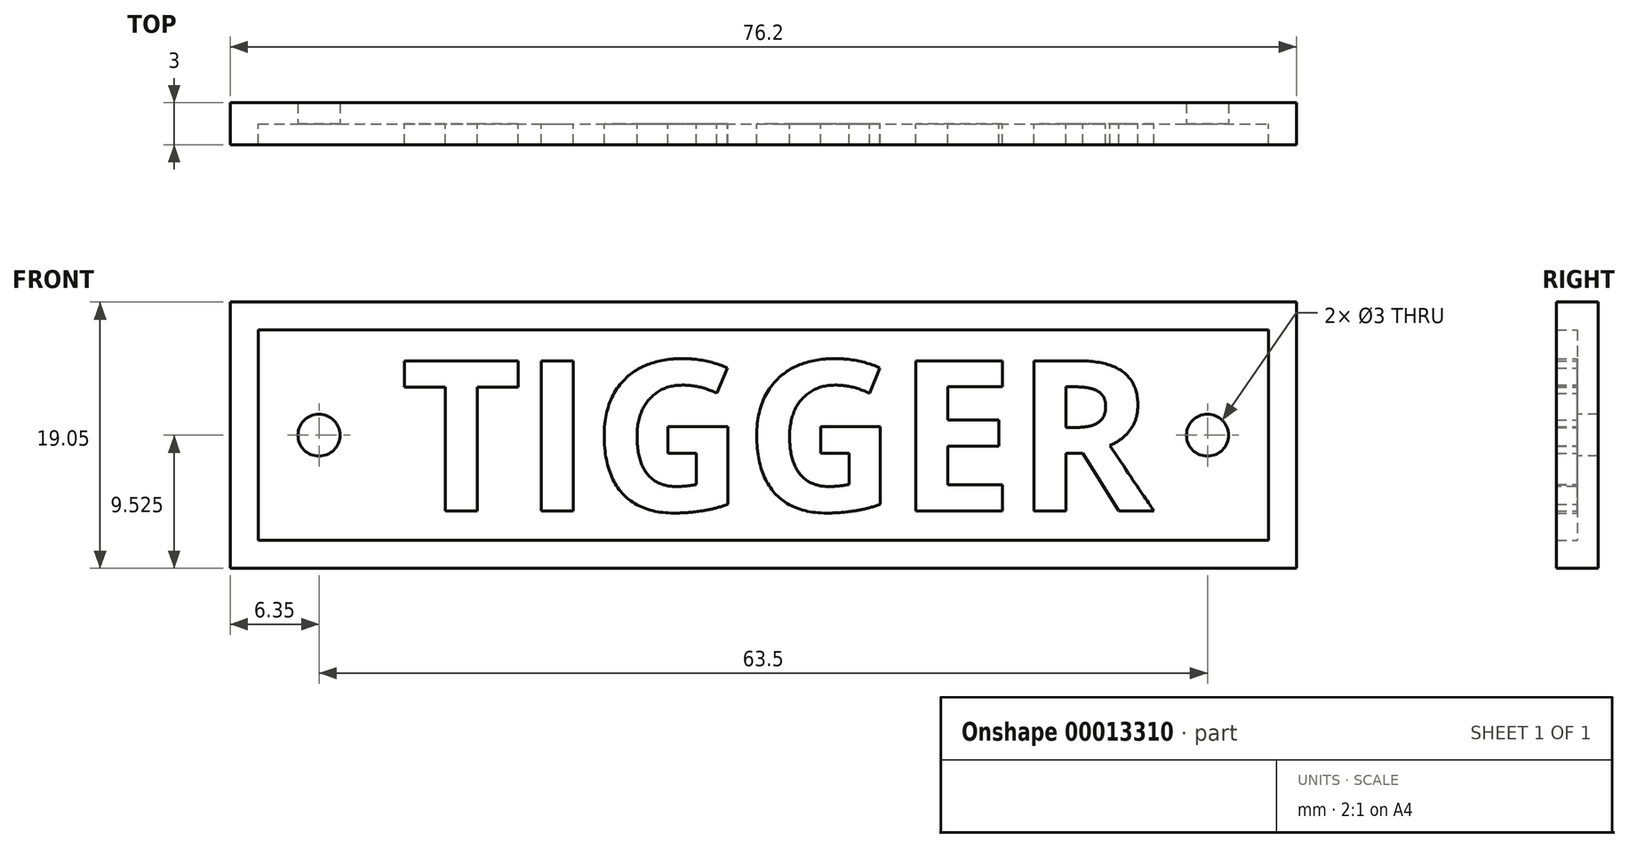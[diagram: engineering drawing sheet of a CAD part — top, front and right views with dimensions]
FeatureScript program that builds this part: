
annotation { "Feature Type Name" : "Feature", "Feature Type Description" : "" }
export const myFeature = defineFeature(function(context is Context, id is Id, definition is map)
    precondition{}
    {
        {
            var Q0;
            Q0=qCreatedBy(makeId("Front.planeOp"),FACE);
            var sketch = newSketch(context, id + "F0", { "sketchPlane" : qUnion([Q0])});
            skLineSegment(sketch, "E0.bottom", {"start": v(76.2, 19.05) * mm, "end": v(0, 19.05) * mm});
            skLineSegment(sketch, "E0.top", {"start": v(76.2, 0) * mm, "end": v(0, 0) * mm});
            skLineSegment(sketch, "E0.left", {"start": v(76.2, 19.05) * mm, "end": v(76.2, 0) * mm});
            skLineSegment(sketch, "E0.right", {"start": v(0, 19.05) * mm, "end": v(0, 0) * mm});
            skSolve(sketch);
        }
        {
            var Q0;
            Q0=qSketchRegion(id+"F0",true);
            extrude(context, id + "F1", {"entities" : qUnion([Q0]), "depth" : 1.5 * mm});
        }
        {
            var Q0;
            Q0=makeQuery(id+"F1.opExtrude","CAP_FACE",FACE,{"disambiguationData":[OSD([sQuery(id+"F0.wireOp",EDGE,"E0.bottom"),sQuery(id+"F0.wireOp",EDGE,"E0.top"),sQuery(id+"F0.wireOp",EDGE,"E0.left"),sQuery(id+"F0.wireOp",EDGE,"E0.right")])],"isStart":false});
            var sketch = newSketch(context, id + "F2", { "sketchPlane" : qUnion([Q0])});
            skLineSegment(sketch, "E1.bottom", {"start": v(0, 0) * mm, "end": v(76.2, 0) * mm});
            skLineSegment(sketch, "E1.top", {"start": v(0, 19.05) * mm, "end": v(76.2, 19.05) * mm});
            skLineSegment(sketch, "E1.left", {"start": v(0, 0) * mm, "end": v(0, 19.05) * mm});
            skLineSegment(sketch, "E1.right", {"start": v(76.2, 0) * mm, "end": v(76.2, 19.05) * mm});
            skLineSegment(sketch, "E2.bottom", {"start": v(2, 17.05) * mm, "end": v(74.2, 17.05) * mm});
            skLineSegment(sketch, "E2.top", {"start": v(2, 2) * mm, "end": v(74.2, 2) * mm});
            skLineSegment(sketch, "E2.left", {"start": v(2, 17.05) * mm, "end": v(2, 2) * mm});
            skLineSegment(sketch, "E2.right", {"start": v(74.2, 17.05) * mm, "end": v(74.2, 2) * mm});
            skSolve(sketch);
        }
        {
            var Q0;
            Q0=qSketchRegion(id+"F2",true);
            extrude(context, id + "F3", {"entities" : qUnion([Q0]), "operationType" : NewBodyOperationType.ADD, "depth" : 1.5 * mm});
        }
        {
            var Q0;
            Q0=makeQuery(id+"F1.opExtrude","CAP_FACE",FACE,{"disambiguationData":[OSD([sQuery(id+"F0.wireOp",EDGE,"E0.bottom"),sQuery(id+"F0.wireOp",EDGE,"E0.top"),sQuery(id+"F0.wireOp",EDGE,"E0.left"),sQuery(id+"F0.wireOp",EDGE,"E0.right")])],"isStart":false});
            var sketch = newSketch(context, id + "F4", { "sketchPlane" : qUnion([Q0])});
            skLineSegment(sketch, "E3.bottom", {"start": v(12.16, 14.95) * mm, "end": v(66.03, 14.95) * mm});
            skLineSegment(sketch, "E3.left", {"start": v(12.16, 14.95) * mm, "end": v(12.16, 4.1) * mm});
            skText(sketch, "E4", { "text": "TIGGER", "fontName": "OpenSans-Bold.ttf"});
            const initialGuessF4  = {"E4": [0.01216, 0.0041, 1, 0, 0.01084]};
            skSetInitialGuess(sketch, initialGuessF4);
            skSolve(sketch);
        }
        {
            var Q0;
            Q0=qSketchRegion(id+"F4",true);
            extrude(context, id + "F5", {"entities" : qUnion([Q0]), "operationType" : NewBodyOperationType.ADD, "depth" : 1.5 * mm});
        }
        {
            var Q0;
            Q0=makeQuery(id+"F5.boolean.opBoolean","SPLIT",FACE,{"disambiguationData":[TD([makeQuery(id+"F3.opExtrude","SWEPT_FACE",FACE,{"disambiguationData":[OSD([sQuery(id+"F2.wireOp",EDGE,"E2.bottom")])]})])],"derivedFrom":makeQuery(id+"F1.opExtrude","CAP_FACE",FACE,{"disambiguationData":[OSD([sQuery(id+"F0.wireOp",EDGE,"E0.bottom"),sQuery(id+"F0.wireOp",EDGE,"E0.top"),sQuery(id+"F0.wireOp",EDGE,"E0.left"),sQuery(id+"F0.wireOp",EDGE,"E0.right")])],"isStart":false})});
            var sketch = newSketch(context, id + "F6", { "sketchPlane" : qUnion([Q0])});
            skCircle(sketch, "E5", {"center": v(6.35, 9.53) * mm, "radius": 1.5 * mm});
            skPoint(sketch, "E5.centerSnap0", {"position": v(2, 9.53) * mm});
            skCircle(sketch, "E6", {"center": v(69.85, 9.53) * mm, "radius": 1.5 * mm});
            skSolve(sketch);
        }
        {
            var Q0;
            Q0=qSketchRegion(id+"F6",true);
            extrude(context, id + "F7", {"entities" : qUnion([Q0]), "operationType" : NewBodyOperationType.REMOVE, "endBound" : BoundingType.THROUGH_ALL, "oppositeDirection" : true, "depth" : 25.4 * mm});
        }
    });
